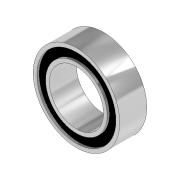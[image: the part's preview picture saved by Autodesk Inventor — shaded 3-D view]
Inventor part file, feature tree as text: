
AUTODESK INVENTOR PART (.ipt)
format: ipt  version: 2020 (Build 240168000, 168)  size: 124,928 bytes
history: native  units: in
note: dims shown in document units (in); Inventor stores cm internally (conversion verified against a paired STEP export)
features: extrude x3, sketch x3, projected_geometry x1
ambient origin geometry x8: Origin, YZ Plane, XZ Plane, XY Plane, X Axis, Y Axis, Z Axis, Center Point
bodies: Solid1 (feature_tree)
feature tree (7):
  extrude  "Extrusion1"  Depth=0.315in
  extrude  "Extrusion2"  Depth=0.0984in
  extrude  "Extrusion3"  Depth=0.0079in TaperAngle=0.0deg
  sketch  "Sketch1"  dims[d0=0.1969in d1=0.315in]
  sketch  "Sketch2"  dims[d2=0.0984in d3=0.0in d4=0.0138in]
  projected_geometry  "Projected Loop1"
  sketch  "Sketch3"  dims[d5=0.0138in d6=0.0079in d7=0.0in d8=0.0079in d9=0.0in]
